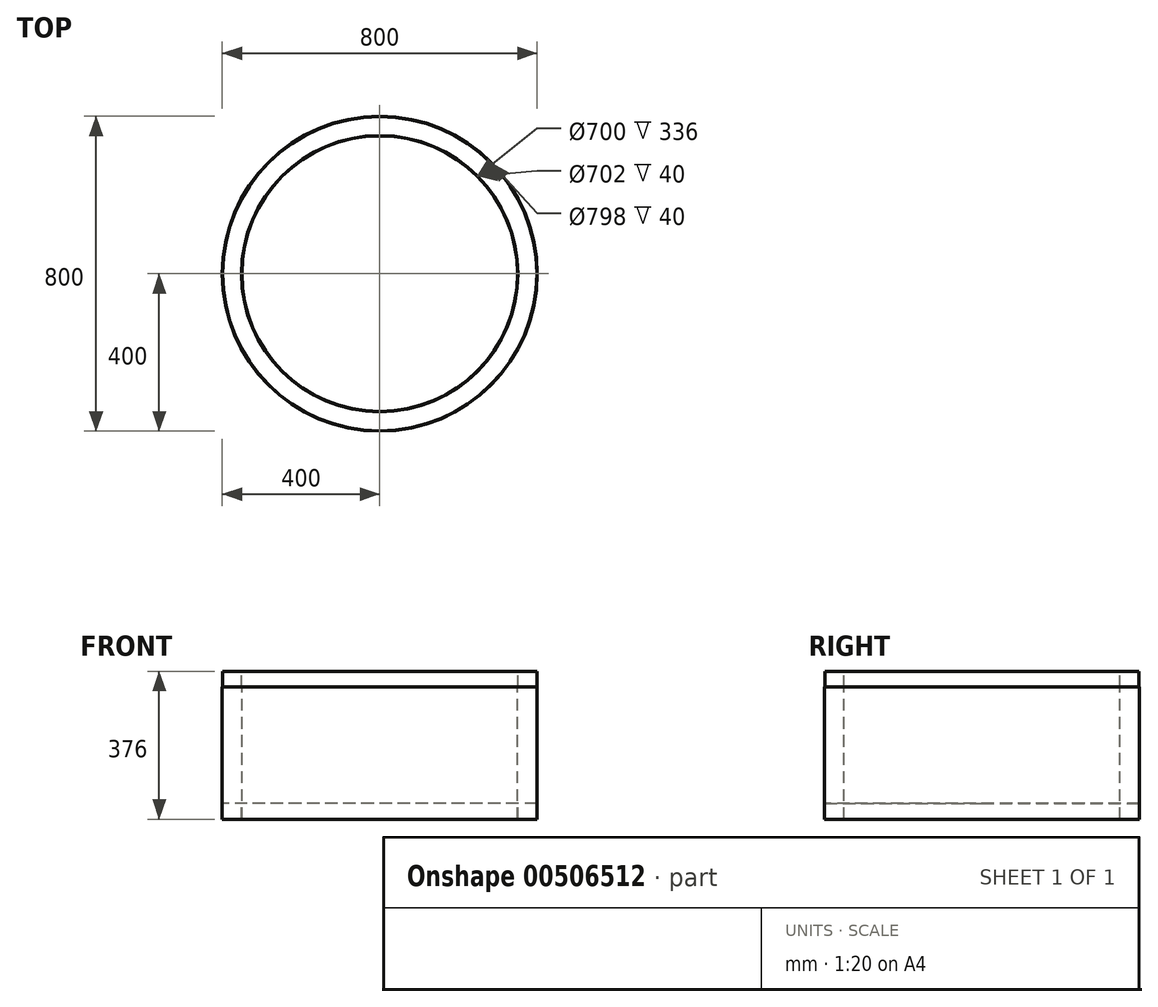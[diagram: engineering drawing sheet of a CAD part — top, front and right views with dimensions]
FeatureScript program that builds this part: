
annotation { "Feature Type Name" : "Feature", "Feature Type Description" : "" }
export const myFeature = defineFeature(function(context is Context, id is Id, definition is map)
    precondition{}
    {
        {
            var Q0;
            Q0=qCreatedBy(makeId("Front.planeOp"),FACE);
            var sketch = newSketch(context, id + "F0", { "sketchPlane" : qUnion([Q0])});
            skLineSegment(sketch, "E0", {"start": v(0, 74.87) * mm, "end": v(0, -73.71) * mm, "construction": true});
            skLineSegment(sketch, "E1", {"start": v(0, 374.84) * mm, "end": v(0, -528.94) * mm, "construction": true});
            skLineSegment(sketch, "E2", {"start": v(-350, -489.75) * mm, "end": v(-350, -153.75) * mm});
            skLineSegment(sketch, "E3", {"start": v(-350, -153.75) * mm, "end": v(-351, -153.75) * mm});
            skLineSegment(sketch, "E4", {"start": v(-351, -153.75) * mm, "end": v(-351, -113.75) * mm});
            skLineSegment(sketch, "E5", {"start": v(-351, -113.75) * mm, "end": v(-399, -113.75) * mm});
            skLineSegment(sketch, "E6", {"start": v(-399, -113.75) * mm, "end": v(-399, -153.75) * mm});
            skLineSegment(sketch, "E7", {"start": v(-399, -153.75) * mm, "end": v(-400, -153.75) * mm});
            skLineSegment(sketch, "E8", {"start": v(-400, -153.75) * mm, "end": v(-400, -489.75) * mm});
            skLineSegment(sketch, "E9", {"start": v(-400, -489.75) * mm, "end": v(-399, -489.75) * mm});
            skLineSegment(sketch, "E10", {"start": v(-399, -489.75) * mm, "end": v(-399, -449.75) * mm});
            skLineSegment(sketch, "E11", {"start": v(-399, -449.75) * mm, "end": v(-351, -449.75) * mm});
            skLineSegment(sketch, "E12", {"start": v(-351, -449.75) * mm, "end": v(-351, -489.75) * mm});
            skLineSegment(sketch, "E13", {"start": v(-351, -489.75) * mm, "end": v(-350, -489.75) * mm});
            skSolve(sketch);
        }
        {
            var Q0;
            Q0=qSketchRegion(id+"F0",true);
            var Q1;
            Q1=sQuery(id+"F0.wireOp",EDGE,"E1");
            revolve(context, id + "F1", {"entities" : qUnion([Q0]), "axis" : qUnion([Q1]), "revolveType" : RevolveType.FULL});
        }
    });
